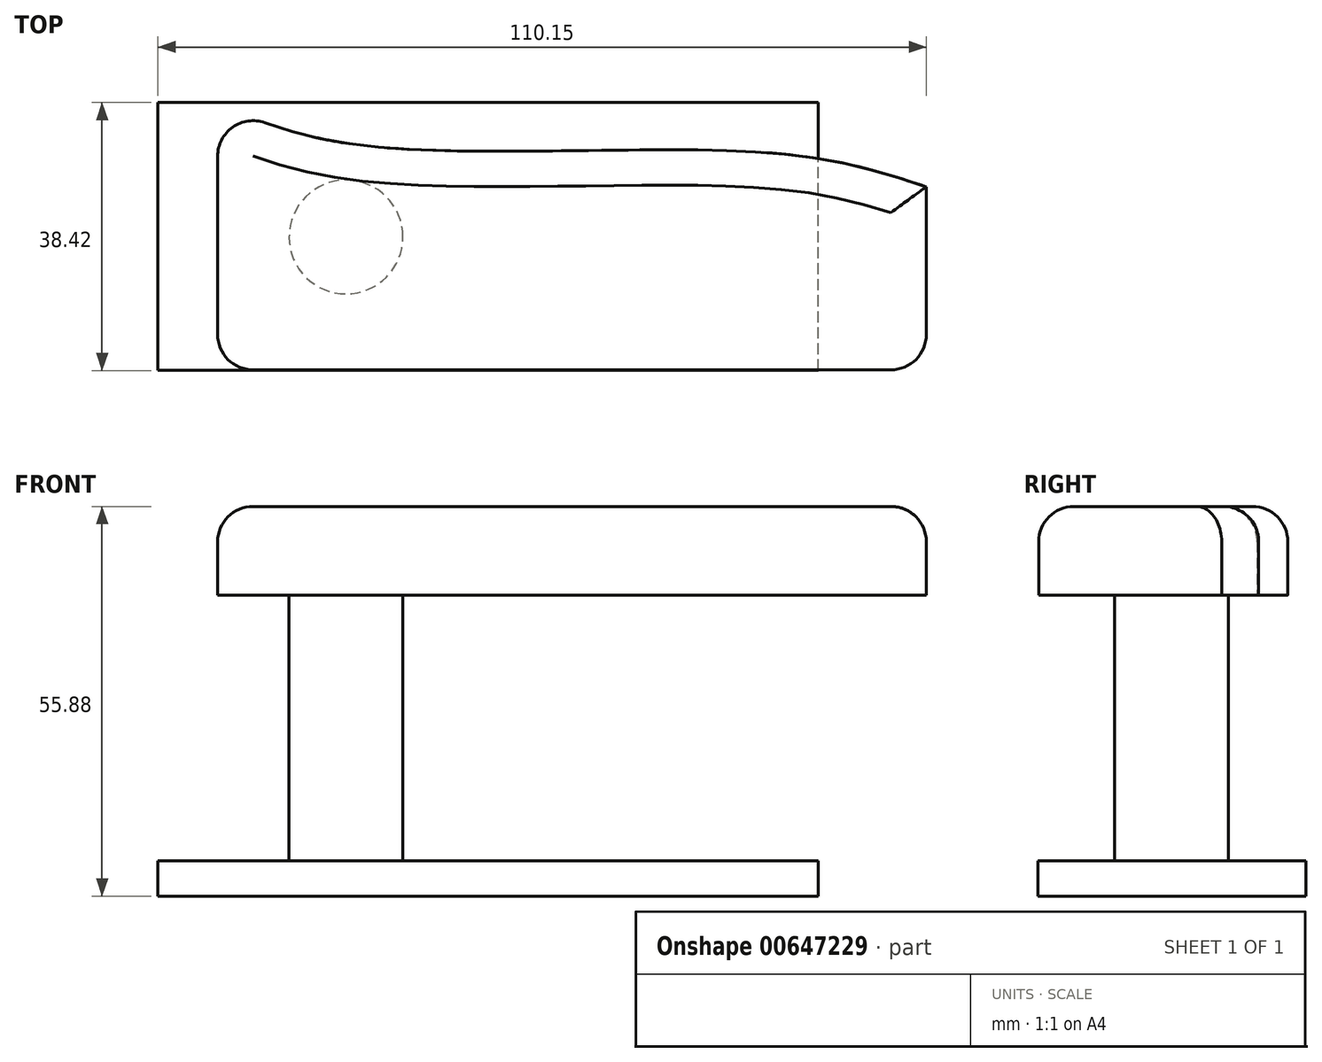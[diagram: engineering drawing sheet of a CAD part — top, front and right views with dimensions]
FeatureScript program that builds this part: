
annotation { "Feature Type Name" : "Feature", "Feature Type Description" : "" }
export const myFeature = defineFeature(function(context is Context, id is Id, definition is map)
    precondition{}
    {
        {
            var Q0;
            Q0=qCreatedBy(makeId("Top.planeOp"),FACE);
            var sketch = newSketch(context, id + "F0", { "sketchPlane" : qUnion([Q0])});
            skLineSegment(sketch, "E0.bottom", {"start": v(-50.8, 19.05) * mm, "end": v(50.8, 19.05) * mm});
            skLineSegment(sketch, "E0.top", {"start": v(-50.8, -19.05) * mm, "end": v(50.8, -19.05) * mm});
            skLineSegment(sketch, "E0.left", {"start": v(-50.8, 19.05) * mm, "end": v(-50.8, -19.05) * mm});
            skLineSegment(sketch, "E0.right", {"start": v(50.8, 19.05) * mm, "end": v(50.8, -19.05) * mm});
            skSolve(sketch);
        }
        {
            var Q0;
            Q0 = qSketchRegion(id + "F0", true);
            extrude(context, id + "F1", {"entities" : qUnion([Q0]), "depth" : 12.7 * mm, "offsetDistance" : 25.4 * mm});
        }
        {
            var Q0;
            Q0=makeQuery(id+"F1.opExtrude","CAP_FACE",FACE,{"disambiguationData":[OSD([sQuery(id+"F0.wireOp",EDGE,"E0.bottom"),sQuery(id+"F0.wireOp",EDGE,"E0.top"),sQuery(id+"F0.wireOp",EDGE,"E0.left"),sQuery(id+"F0.wireOp",EDGE,"E0.right")])],"isStart":false});
            var sketch = newSketch(context, id + "F2", { "sketchPlane" : qUnion([Q0])});
            skFitSpline(sketch, "E1", {"points": [v(-50.8, 19.05) * mm, v(-28.92, 13) * mm, v(28.22, 12.08) * mm, v(50.8, 7.2) * mm], "startDerivative": vector(64.65, -26.91) * mm, "endDerivative": vector(66.63, -21.95) * mm});
            skLineSegment(sketch, "E2", {"start": v(-50.8, 19.05) * mm, "end": v(-50.8, 29.5) * mm});
            skLineSegment(sketch, "E3", {"start": v(-50.8, 29.5) * mm, "end": v(51.44, 29.5) * mm});
            skLineSegment(sketch, "E4", {"start": v(51.44, 29.5) * mm, "end": v(50.8, 7.2) * mm});
            skSolve(sketch);
        }
        {
            var Q0;
            Q0 = qSketchRegion(id + "F2", true);
            extrude(context, id + "F3", {"entities" : qUnion([Q0]), "operationType" : NewBodyOperationType.REMOVE, "oppositeDirection" : true, "depth" : 25.4 * mm, "offsetDistance" : 25.4 * mm});
        }
        {
            var Q0;
            Q0=makeQuery(id+"F1.opExtrude","CAP_EDGE",EDGE,{"disambiguationData":[OSD([sQuery(id+"F0.wireOp",EDGE,"E0.top")])],"isStart":false});
            var Q1;
            Q1=makeQuery(id+"F1.opExtrude","CAP_EDGE",EDGE,{"disambiguationData":[OSD([sQuery(id+"F0.wireOp",EDGE,"E0.right")])],"isStart":false});
            var Q2;
            Q2=makeQuery(id+"F1.opExtrude","CAP_EDGE",EDGE,{"disambiguationData":[OSD([sQuery(id+"F0.wireOp",EDGE,"E0.bottom")])],"isStart":false});
            var Q3;
            Q3=makeQuery(id+"F1.opExtrude","CAP_FACE",FACE,{"disambiguationData":[OSD([sQuery(id+"F0.wireOp",EDGE,"E0.bottom"),sQuery(id+"F0.wireOp",EDGE,"E0.top"),sQuery(id+"F0.wireOp",EDGE,"E0.left"),sQuery(id+"F0.wireOp",EDGE,"E0.right")])],"isStart":false});
            fillet(context, id + "F4", {"entities" : qUnion([Q0, Q1, Q2, Q3]), "radius" : 5.08 * mm, "tangentPropagation" : true, "allowEdgeOverflow" : false});
        }
        {
            var Q0;
            Q0=qCreatedBy(makeId("Top.planeOp"),FACE);
            var sketch = newSketch(context, id + "F5", { "sketchPlane" : qUnion([Q0])});
            skCircle(sketch, "E5", {"center": v(-32.4, 0) * mm, "radius": 8.16 * mm});
            skSolve(sketch);
        }
        {
            var Q0;
            Q0 = qSketchRegion(id + "F5", true);
            extrude(context, id + "F6", {"entities" : qUnion([Q0]), "operationType" : NewBodyOperationType.ADD, "oppositeDirection" : true, "depth" : 38.1 * mm, "offsetDistance" : 25.4 * mm});
        }
        {
            var Q0;
            Q0=makeQuery(id+"F6.opExtrude","CAP_FACE",FACE,{"disambiguationData":[OSD([sQuery(id+"F5.wireOp",EDGE,"E5")])],"isStart":false});
            var sketch = newSketch(context, id + "F7", { "sketchPlane" : qUnion([Q0])});
            skLineSegment(sketch, "E6.bottom", {"start": v(-59.35, 19.15) * mm, "end": v(35.28, 19.15) * mm});
            skLineSegment(sketch, "E6.top", {"start": v(-59.35, -19.27) * mm, "end": v(35.28, -19.27) * mm});
            skLineSegment(sketch, "E6.left", {"start": v(-59.35, 19.15) * mm, "end": v(-59.35, -19.27) * mm});
            skLineSegment(sketch, "E6.right", {"start": v(35.28, 19.15) * mm, "end": v(35.28, -19.27) * mm});
            skSolve(sketch);
        }
        {
            var Q0;
            Q0 = qSketchRegion(id + "F7", true);
            extrude(context, id + "F8", {"entities" : qUnion([Q0]), "operationType" : NewBodyOperationType.ADD, "depth" : 5.08 * mm, "offsetDistance" : 25.4 * mm});
        }
        {
            var Q0;
            Q0=makeQuery(id+"F1.opExtrude","SWEPT_EDGE",EDGE,{"disambiguationData":[OSD([sQuery(id+"F0.wireOp",EDGE,"E0.top"),sQuery(id+"F0.wireOp",EDGE,"E0.right")])]});
            var Q1;
            Q1=makeQuery(id+"F3.boolean.opBoolean","COPY",EDGE,{"derivedFrom":makeQuery(id+"F3.opExtrude","SWEPT_EDGE",EDGE,{"disambiguationData":[OSD([sQuery(id+"F0.wireOp",EDGE,"E0.right"),sQuery(id+"F2.wireOp",EDGE,"E1"),sQuery(id+"F2.wireOp",EDGE,"E4")])]})});
            var Q2;
            Q2=makeQuery(id+"F1.opExtrude","SWEPT_EDGE",EDGE,{"disambiguationData":[OSD([sQuery(id+"F0.wireOp",EDGE,"E0.top"),sQuery(id+"F0.wireOp",EDGE,"E0.left")])]});
            var Q3;
            {var subQ0=sQuery(id+"F0.wireOp",EDGE,"E0.left");var subQ1=sQuery(id+"F0.wireOp",EDGE,"E0.bottom");Q3=makeQuery(id+"F3.boolean.opBoolean","MERGE",EDGE,{"derivedFrom":[makeQuery(id+"F1.opExtrude","SWEPT_EDGE",EDGE,{"disambiguationData":[OSD([subQ1,subQ0])]}),makeQuery(id+"F3.opExtrude","SWEPT_EDGE",EDGE,{"disambiguationData":[OSD([subQ1,subQ0,sQuery(id+"F2.wireOp",EDGE,"E1"),sQuery(id+"F2.wireOp",EDGE,"E2")])]})]});}
            fillet(context, id + "F9", {"entities" : qUnion([Q0, Q1, Q2, Q3]), "radius" : 5.08 * mm, "tangentPropagation" : true, "allowEdgeOverflow" : false});
        }
    });
